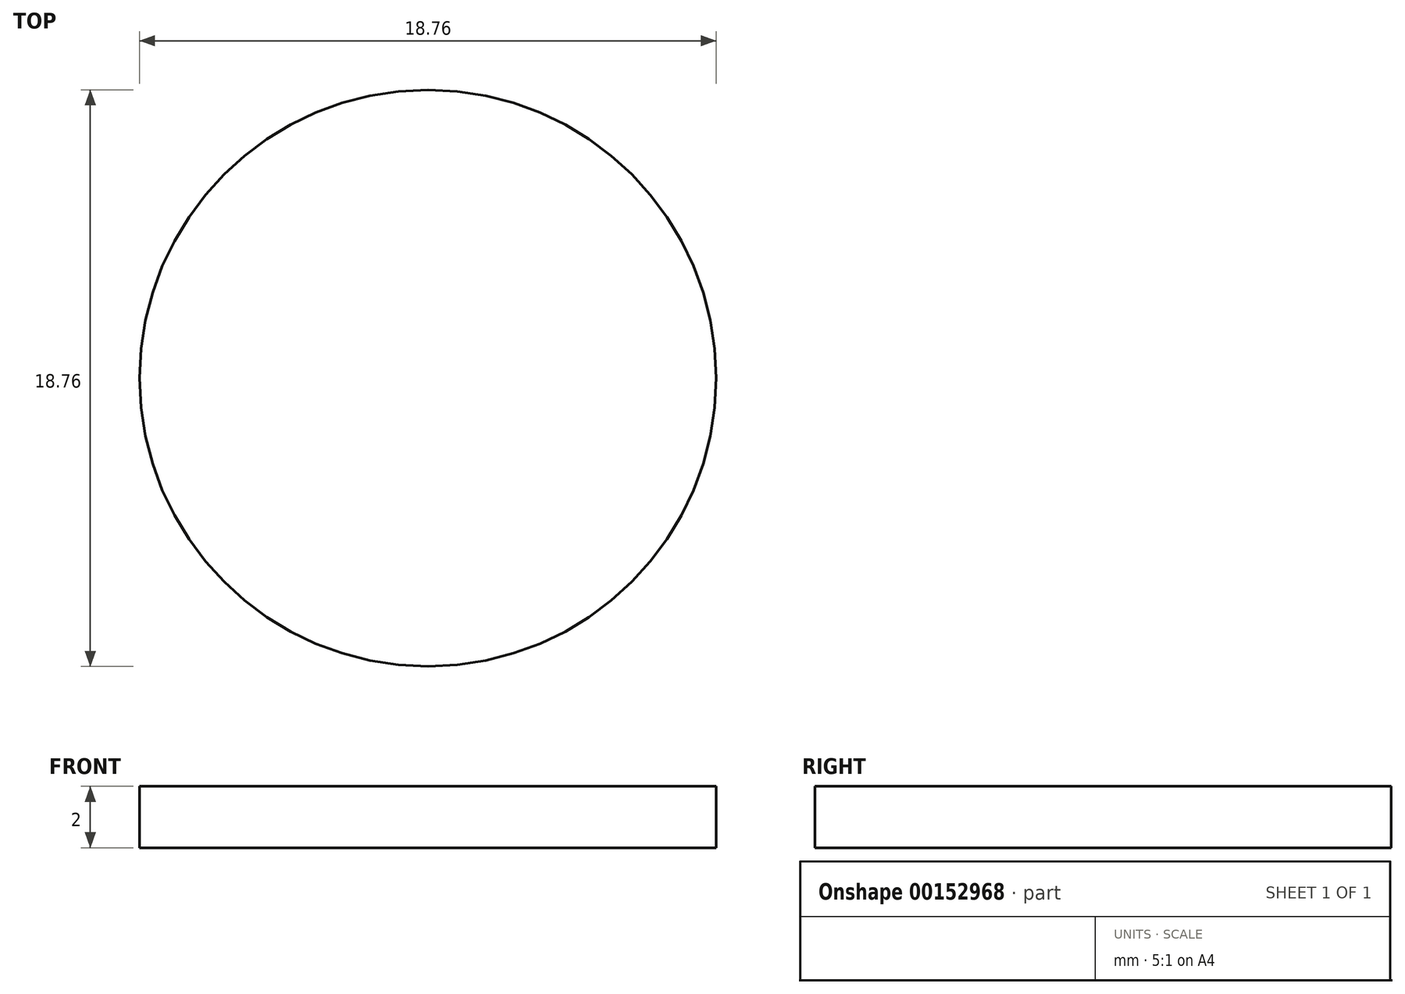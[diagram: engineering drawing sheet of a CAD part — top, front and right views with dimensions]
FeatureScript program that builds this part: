
annotation { "Feature Type Name" : "Feature", "Feature Type Description" : "" }
export const myFeature = defineFeature(function(context is Context, id is Id, definition is map)
    precondition{}
    {
        {
            var Q0;
            Q0=qCreatedBy(makeId("Top.planeOp"),FACE);
            var sketch = newSketch(context, id + "F0", { "sketchPlane" : qUnion([Q0])});
            skCircle(sketch, "E0", {"center": v(0, 0) * mm, "radius": 7.88 * mm});
            skCircle(sketch, "E1.0", {"center": v(0, 0) * mm, "radius": 9.38 * mm});
            skSolve(sketch);
        }
        {
            var Q0;
            Q0 = qSketchRegion(id + "F0", true);
            var Q1;
            Q1=makeQuery(id+"F0.imprint","IMPRINT",FACE,{"disambiguationData":[TD([[makeQuery(id+"F0.imprint","IMPRINT",EDGE,{"derivedFrom":sQuery(id+"F0.wireOp",EDGE,"E0")}),1.0]])]});
            extrude(context, id + "F1", {"entities" : qUnion([Q0, Q1]), "oppositeDirection" : true, "depth" : 2 * mm});
        }
    });
